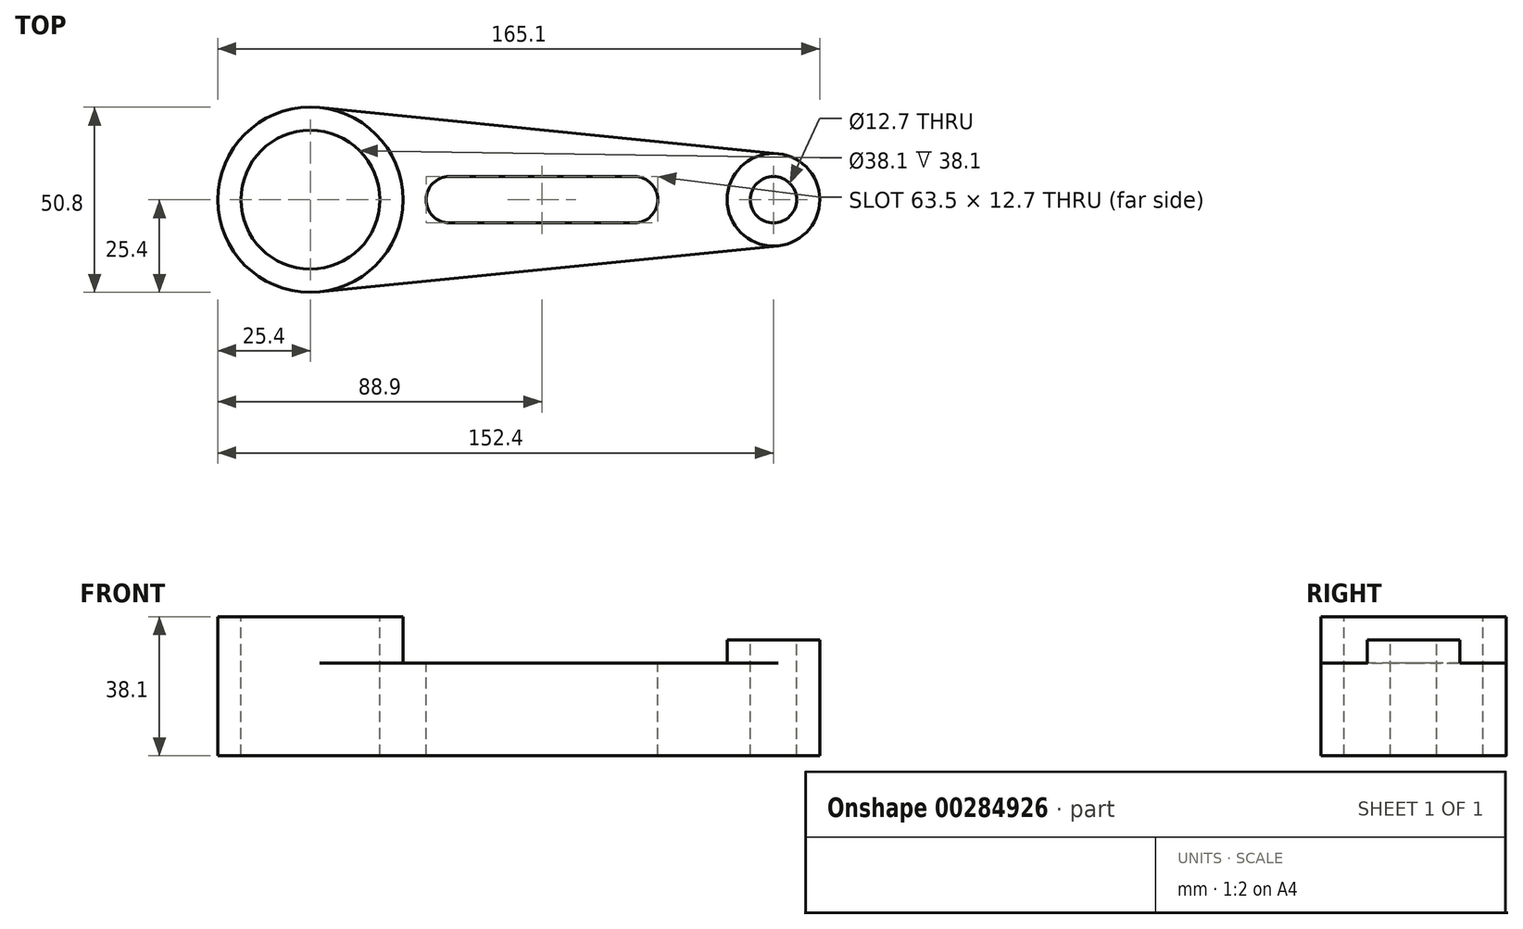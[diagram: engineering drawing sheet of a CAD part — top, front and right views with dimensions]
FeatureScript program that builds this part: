
annotation { "Feature Type Name" : "Feature", "Feature Type Description" : "" }
export const myFeature = defineFeature(function(context is Context, id is Id, definition is map)
    precondition{}
    {
        {
            var Q0;
            Q0=qCreatedBy(makeId("Top.planeOp"),FACE);
            var sketch = newSketch(context, id + "F0", { "sketchPlane" : qUnion([Q0])});
            skLineSegment(sketch, "E0", {"start": v(-38.1, 0) * mm, "end": v(88.9, 0) * mm, "construction": true});
            skCircle(sketch, "E1", {"center": v(-38.1, 0) * mm, "radius": 25.4 * mm});
            skCircle(sketch, "E2", {"center": v(-38.1, 0) * mm, "radius": 19.05 * mm});
            skCircle(sketch, "E3", {"center": v(88.9, 0) * mm, "radius": 6.35 * mm});
            skCircle(sketch, "E4", {"center": v(88.9, 0) * mm, "radius": 12.7 * mm});
            skLineSegment(sketch, "E5", {"start": v(-35.56, 25.27) * mm, "end": v(90.17, 12.64) * mm});
            skLineSegment(sketch, "E6", {"start": v(-35.56, -25.27) * mm, "end": v(90.17, -12.64) * mm});
            skPoint(sketch, "E7", {"position": v(50.8, 0) * mm});
            skPoint(sketch, "E8", {"position": v(0, 0) * mm});
            skLineSegment(sketch, "E9", {"start": v(0, 6.35) * mm, "end": v(50.8, 6.35) * mm});
            skLineSegment(sketch, "E10", {"start": v(0, -6.35) * mm, "end": v(50.8, -6.35) * mm});
            skCircle(sketch, "E11", {"center": v(0, 0) * mm, "radius": 6.35 * mm});
            skCircle(sketch, "E12", {"center": v(50.8, 0) * mm, "radius": 6.35 * mm});
            skSolve(sketch);
        }
        {
            var Q0;
            Q0=makeQuery(id+"F0.imprint","IMPRINT",FACE,{"disambiguationData":[TD([[makeQuery(id+"F0.imprint","IMPRINT",EDGE,{"derivedFrom":sQuery(id+"F0.wireOp",EDGE,"E2")}),-1.0]])]});
            var Q1;
            {var subQ1=sQuery(id+"F0.wireOp",EDGE,"E5");Q1=makeQuery(id+"F0.imprint","IMPRINT",FACE,{"disambiguationData":[TD([[makeQuery(id+"F0.imprint","IMPRINT",EDGE,{"derivedFrom":subQ1}),-1.0]])]});}
            var Q2;
            Q2=makeQuery(id+"F0.imprint","IMPRINT",FACE,{"disambiguationData":[TD([[makeQuery(id+"F0.imprint","IMPRINT",EDGE,{"derivedFrom":sQuery(id+"F0.wireOp",EDGE,"E3")}),-1.0]])]});
            extrude(context, id + "F1", {"entities" : qUnion([Q0, Q1, Q2]), "oppositeDirection" : true, "depth" : 38.1 * mm});
        }
        {
            var Q0;
            {var subQ1=sQuery(id+"F0.wireOp",EDGE,"E5");Q0=makeQuery(id+"F0.imprint","IMPRINT",FACE,{"disambiguationData":[TD([[makeQuery(id+"F0.imprint","IMPRINT",EDGE,{"derivedFrom":subQ1}),-1.0]])]});}
            extrude(context, id + "F2", {"entities" : qUnion([Q0]), "operationType" : NewBodyOperationType.REMOVE, "oppositeDirection" : true, "depth" : 12.7 * mm});
        }
        {
            var Q0;
            Q0=makeQuery(id+"F0.imprint","IMPRINT",FACE,{"disambiguationData":[TD([[makeQuery(id+"F0.imprint","IMPRINT",EDGE,{"derivedFrom":sQuery(id+"F0.wireOp",EDGE,"E3")}),-1.0]])]});
            extrude(context, id + "F3", {"entities" : qUnion([Q0]), "operationType" : NewBodyOperationType.REMOVE, "oppositeDirection" : true, "depth" : 6.35 * mm});
        }
    });
